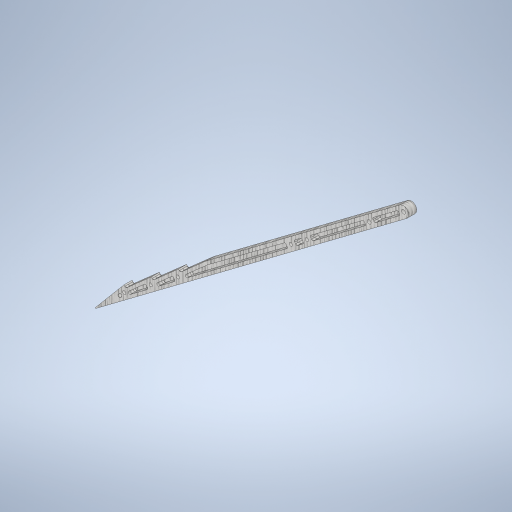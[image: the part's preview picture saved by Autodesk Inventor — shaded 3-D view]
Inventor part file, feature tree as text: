
AUTODESK INVENTOR PART (.ipt)
format: ipt  version: 2023 (Build 270158030, 158C)  size: 1,088,000 bytes
history: native  units: mm
features: sketch x12, extrude x9, projected_geometry x8, other x6, fillet x3, hole x1, reference x1
ambient origin geometry x8: Origin, YZ Plane, XZ Plane, XY Plane, X Axis, Y Axis, Z Axis, Center Point
bodies: Body1 (feature_tree)
feature tree (40):
  other  "ソリッド1"
  extrude  "押し出し1"  Depth=1.0mm TaperAngle=15.0deg
  extrude  "押し出し2"  Depth=6.0mm TaperAngle=0.0deg
  extrude  "押し出し6"  Depth=3.0mm
  fillet  "フィレット3"  Radius=3.0mm
  extrude  "押し出し11"  Depth=3.0mm
  fillet  "フィレット4"  Radius=3.0mm
  extrude  "押し出し12"  Depth=3.0mm
  sketch  "スケッチ15"
  sketch  "スケッチ17"
  sketch  "スケッチ19"
  extrude  "押し出し13"  Depth=3.0mm
  extrude  "押し出し14"  Depth=3.0mm
  extrude  "押し出し15"  Depth=25.0mm
  sketch  "スケッチ22"
  extrude  "押し出し16"  Depth=25.0mm
  hole  "穴1"  [1 undecoded]
  fillet  "フィレット5"  Radius=25.0mm
  sketch  "スケッチ24"
  sketch  "スケッチ1"
  sketch  "スケッチ2"
  projected_geometry  "投影ループ1"
  sketch  "スケッチ7"
  projected_geometry  "投影ループ6"
  sketch  "スケッチ13"
  sketch  "スケッチ14"
  projected_geometry  "投影ループ11"
  projected_geometry  "投影ループ12"
  reference  "参照1"
  projected_geometry  "投影ループ14"
  projected_geometry  "投影ループ15"
  sketch  "スケッチ21"
  projected_geometry  "投影ループ16"
  projected_geometry  "投影ループ17"
  sketch  "スケッチ23"
  other  "<userpath>\Documents\SRDC\SRDC\Inventor_2017\2018年機体\2019年3年機体\アーム先端ツイン1.iam"
  other  "アーム先端ツイン1.iam"
  other  "アーム先端返し2.1:1"
  other  "断面エッジを投影1"
  other  "断面エッジを投影2"
note: 1 required parameter value undecoded (feature->parameter linkage not recoverable at this tier; creation-order binding heuristic only, values carry confidence <= 0.55)
